# Revit family: 0047643+0047517 Feilo Sylvania Lighting Fixture START FLAT LO 600 4000K G2 with SUSPENSION KIT
name_source: partatom
category: Lighting Fixtures
revit_build: Autodesk Revit 2017 (Build: 20190507_1515(x64)
units: mm (PartAtom-declared; Revit-internal decimal feet)

## family parameters
Cut with Voids When Loaded = No
Host = Face
Light Source = Yes
OmniClass Number = 23.80.70.00
OmniClass Title = Lighting
Part Type = Normal
Room Calculation Point = No
Round Connector Dimension = Use Diameter
Shared = No

## types (1)
- 0047643 START FLAT LO 600 4000K G2
    Apparent Load = 30 VA
    Assembly Code = D5020200
    AssetType = Fixed
    ClassificationName = Uniclass2015
    ClassificationValue = EF_70_80
    Color Filter = 16777215
    Cost = 0 $
    Default Elevation = 1219 mm
    Description = Edge lit LED flat panel LO (low output). Low Flicker, 30 W, Neutral White, 4000 K, 3000 lumens, 102 lm/W, 50000 hours lifetime (L70), PMMA opal diffuser, aluminium frame, steel body, electronic non dimmable driver. (HxWxD) 10.5 x 595 x 595 mm
    Dimming Lamp Color Temperature Shift = <None>
    DocumentationLiterature = http://www.sylvania-lighting.com
    DurationUnit = hours
    ElectricShockClassification = Class II
    Emit Shape Visible in Rendering = No
    Emit from Rectangle Length = 555 mm
    Emit from Rectangle Width = 555 mm
    ExpectedLife = 50000
    Height_FEILO = 11 mm
    IfcExportAs = IfcLightFixtureType
    IfcExportType = IfcLightFixtureType
    ImpactProtectionIndex = IK03
    IngressProtection = IP20
    InputNominalFrequency = 50/60 Hz
    InputVoltage = 220-240V~
    Keynote = 16500
    Lamp = LED
    LampColourRenderingIndex = 80
    LampColourTemperature = 4000 K
    LampMacAdamStep = 3
    LampNominalLuminous = 3000 lm
    LampsType = LED
    Length_FEILO = 595 mm
    LuminousEfficacy = 102 lm/W
    Manufacturer = Feilo Sylvania
    ManufacturerName = Feilo Sylvania
    Material = aluminium housing, pmma diffuser
    Material_1_FEILO = Body-Sylvania-StartFlat-White
    Material_2_FEILO = LED-Sylvania-StartFlat
    Material_3_FEILO = <By Category>
    Material_4_FEILO = <By Category>
    Model = START FLAT LO 600 4000K G2
    ModelNumber = 0047643
    ModelReference = START FLAT LO 600 4000K G2
    Name = START FLAT LO 600 4000K G2
    NominalDepth = 595 mm
    NominalHeight = 11 mm
    NominalLength = 595 mm
    Photometric Web File = 0047643.ies
    PowerConsumption = 30 W
    PowerFactor = 0.9
    RadiusWire_FEILO = 1 mm  [stored 0.00328084 ft]
    SSH1_FEILO = No
    SSH2_FEILO = No
    SSH3_FEILO = No
    SuspensionFromSides_FEILO = 20 mm
    Tilt Angle = -90.00°
    Type Image = <None>
    TypeName = START FLAT LO 600 4000K G2
    URL = http://www.sylvania-lighting.com
    Voltage = 230 V
    Weight = 5.884 kg
    Width_FEILO = 595 mm

note: [stored X ft] marks values corroborated as IEEE doubles in the binary element streams (Revit-internal decimal feet)

## geometry (parser evidence)
native form markers: Sweep x2
no freeform markers — native parametric forms only
